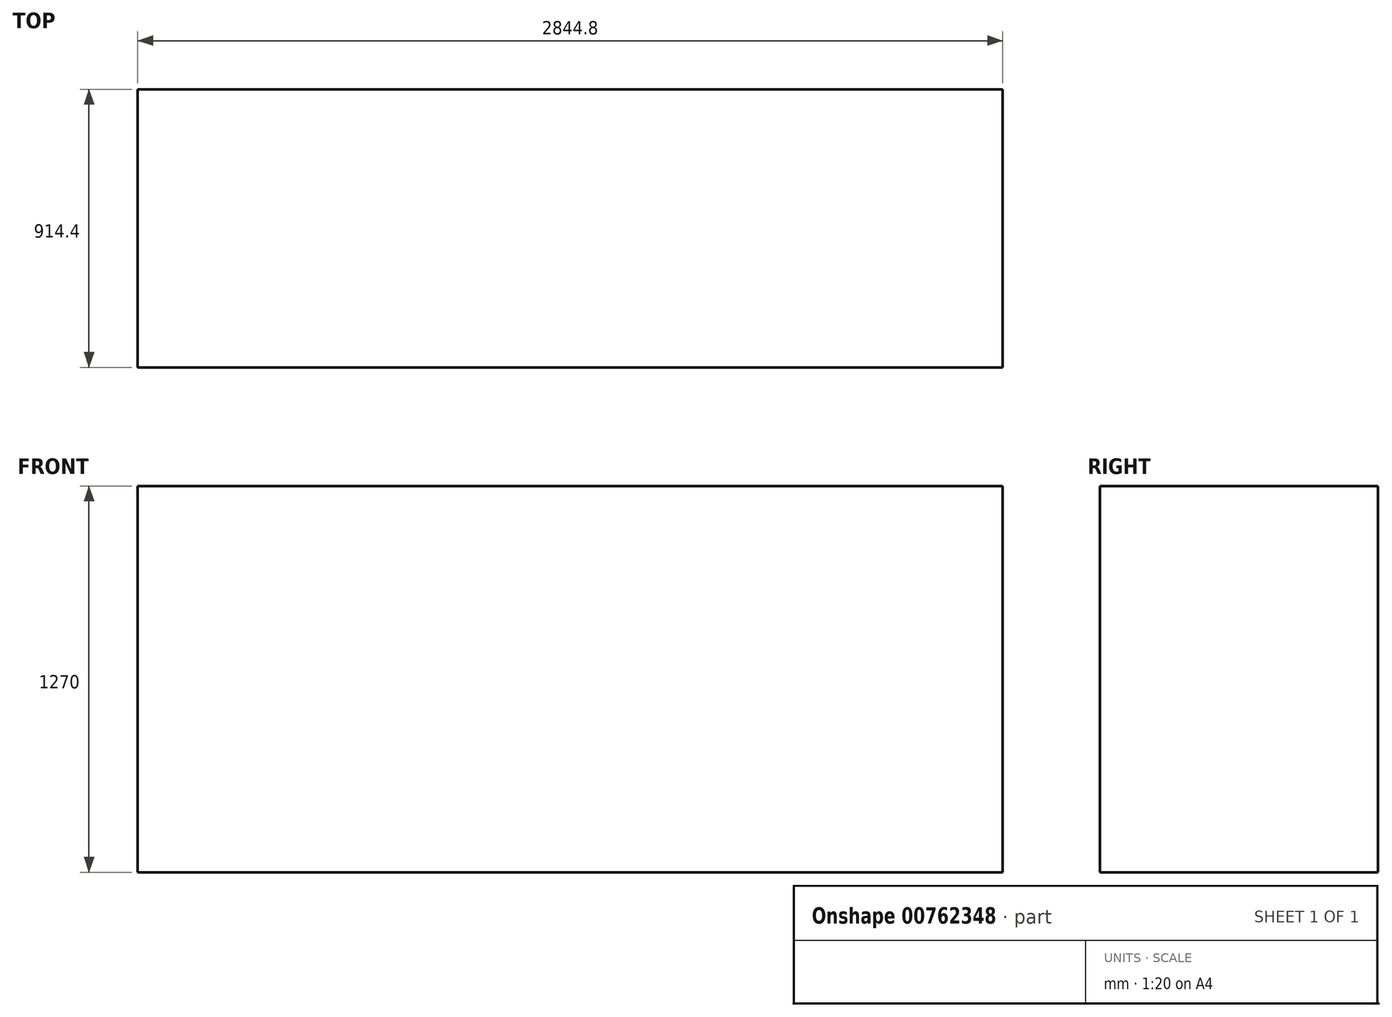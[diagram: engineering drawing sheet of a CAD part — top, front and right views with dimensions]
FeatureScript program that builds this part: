
annotation { "Feature Type Name" : "Feature", "Feature Type Description" : "" }
export const myFeature = defineFeature(function(context is Context, id is Id, definition is map)
    precondition{}
    {
        {
            var Q0;
            Q0=qCreatedBy(makeId("Front.planeOp"),FACE);
            var sketch = newSketch(context, id + "F0", { "sketchPlane" : qUnion([Q0])});
            skLineSegment(sketch, "E0.bottom", {"start": v(0, 0) * mm, "end": v(2844.8, 0) * mm});
            skLineSegment(sketch, "E0.top", {"start": v(0, 1270) * mm, "end": v(2844.8, 1270) * mm});
            skLineSegment(sketch, "E0.left", {"start": v(0, 0) * mm, "end": v(0, 1270) * mm});
            skLineSegment(sketch, "E0.right", {"start": v(2844.8, 0) * mm, "end": v(2844.8, 1270) * mm});
            skSolve(sketch);
        }
        {
            var Q0;
            Q0=makeQuery(id+"F0.imprint","IMPRINT",FACE,{"disambiguationData":[TD([[makeQuery(id+"F0.imprint","IMPRINT",EDGE,{"derivedFrom":sQuery(id+"F0.wireOp",EDGE,"E0.bottom")}),1.0]])]});
            extrude(context, id + "F1", {"entities" : qUnion([Q0]), "depth" : 914.4 * mm, "offsetDistance" : 25.4 * mm});
        }
    });
